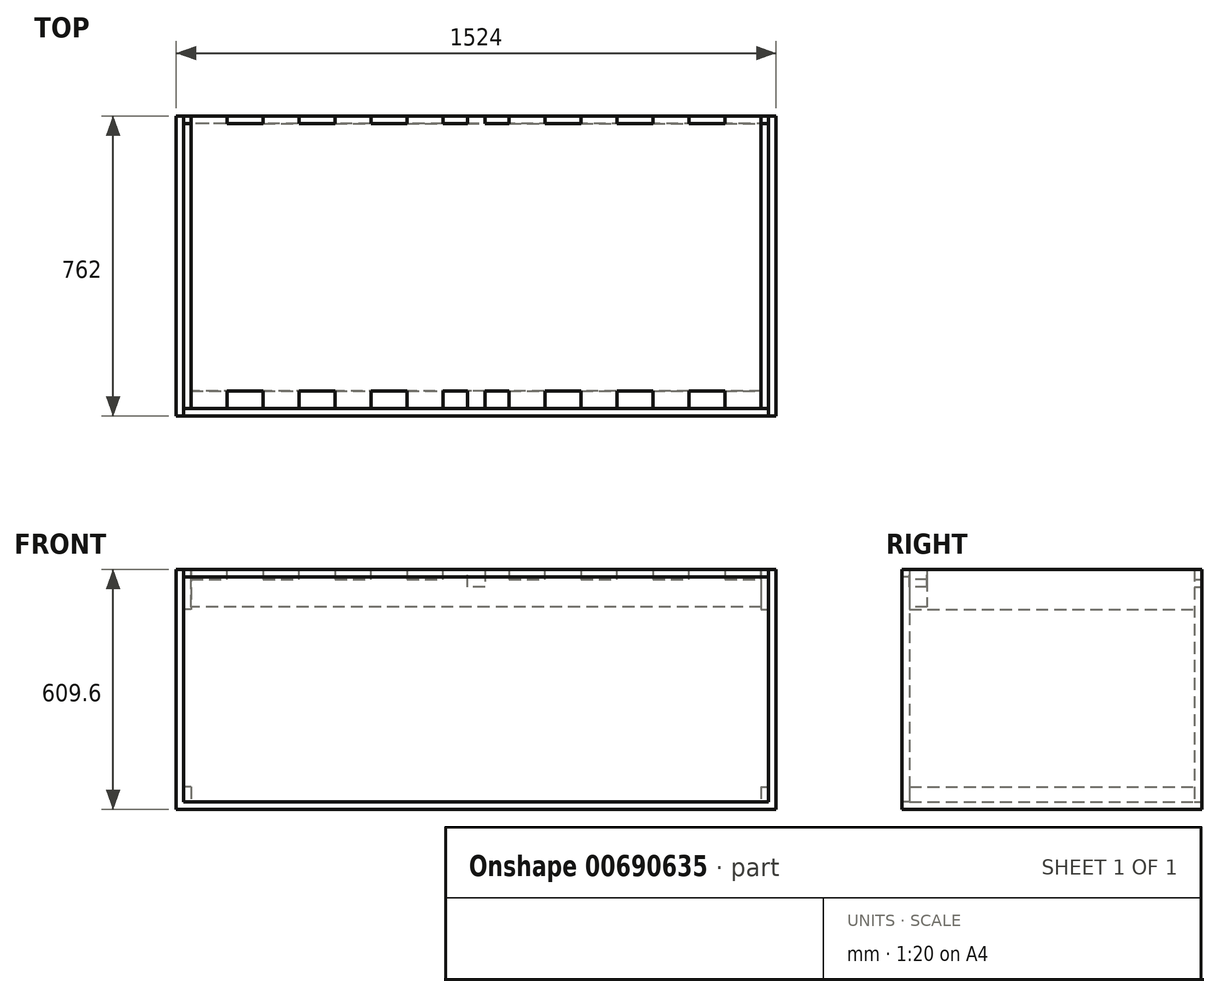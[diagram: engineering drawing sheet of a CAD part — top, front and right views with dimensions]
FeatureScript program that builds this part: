
annotation { "Feature Type Name" : "Feature", "Feature Type Description" : "" }
export const myFeature = defineFeature(function(context is Context, id is Id, definition is map)
    precondition{}
    {
        {
            var Q0;
            Q0=qCreatedBy(makeId("Top.planeOp"),FACE);
            var sketch = newSketch(context, id + "F0", { "sketchPlane" : qUnion([Q0])});
            skLineSegment(sketch, "E0.bottom", {"start": v(-762, -381) * mm, "end": v(762, -381) * mm});
            skLineSegment(sketch, "E0.top", {"start": v(-762, 381) * mm, "end": v(762, 381) * mm});
            skLineSegment(sketch, "E0.left", {"start": v(-762, -381) * mm, "end": v(-762, 381) * mm});
            skLineSegment(sketch, "E0.right", {"start": v(762, -381) * mm, "end": v(762, 381) * mm});
            skPoint(sketch, "E0.middle", {"position": v(0, 0) * mm});
            skSolve(sketch);
        }
        {
            var Q0;
            Q0=makeQuery(id+"F0.imprint","IMPRINT",FACE,{"disambiguationData":[TD([[makeQuery(id+"F0.imprint","IMPRINT",EDGE,{"derivedFrom":sQuery(id+"F0.wireOp",EDGE,"E0.bottom")}),1.0]])]});
            extrude(context, id + "F1", {"entities" : qUnion([Q0]), "oppositeDirection" : true, "depth" : 609.6 * mm, "offsetDistance" : 25.4 * mm});
        }
        {
            var Q0;
            Q0=makeQuery(id+"F1.opExtrude","SWEPT_FACE",FACE,{"disambiguationData":[OSD([sQuery(id+"F0.wireOp",EDGE,"E0.bottom")])]});
            var sketch = newSketch(context, id + "F2", { "sketchPlane" : qUnion([Q0])});
            skLineSegment(sketch, "E1.bottom", {"start": v(-742.95, -19.05) * mm, "end": v(742.95, -19.05) * mm});
            skLineSegment(sketch, "E1.top", {"start": v(-742.95, -590.55) * mm, "end": v(742.95, -590.55) * mm});
            skLineSegment(sketch, "E1.left", {"start": v(-742.95, -19.05) * mm, "end": v(-742.95, -590.55) * mm});
            skLineSegment(sketch, "E1.right", {"start": v(742.95, -19.05) * mm, "end": v(742.95, -590.55) * mm});
            skSolve(sketch);
        }
        {
            var Q0;
            Q0 = qSketchRegion(id + "F2", true);
            extrude(context, id + "F3", {"entities" : qUnion([Q0]), "oppositeDirection" : true, "depth" : 19.05 * mm, "offsetDistance" : 25.4 * mm});
        }
        {
            var Q0;
            Q0=makeQuery(id+"F3.opExtrude","CAP_FACE",FACE,{"disambiguationData":[OSD([sQuery(id+"F2.wireOp",EDGE,"E1.bottom"),sQuery(id+"F2.wireOp",EDGE,"E1.top"),sQuery(id+"F2.wireOp",EDGE,"E1.left"),sQuery(id+"F2.wireOp",EDGE,"E1.right")])],"isStart":false});
            var sketch = newSketch(context, id + "F4", { "sketchPlane" : qUnion([Q0])});
            skLineSegment(sketch, "E2", {"start": v(-723.9, -95.25) * mm, "end": v(723.9, -95.25) * mm});
            skLineSegment(sketch, "E3", {"start": v(723.9, -95.25) * mm, "end": v(723.9, -25.4) * mm});
            skLineSegment(sketch, "E4", {"start": v(723.9, -25.4) * mm, "end": v(632.46, -25.4) * mm});
            skLineSegment(sketch, "E5", {"start": v(632.46, -25.4) * mm, "end": v(632.46, 0) * mm});
            skLineSegment(sketch, "E6", {"start": v(632.46, 0) * mm, "end": v(541.02, 0) * mm});
            skLineSegment(sketch, "E7", {"start": v(541.02, 0) * mm, "end": v(541.02, -25.4) * mm});
            skLineSegment(sketch, "E8", {"start": v(541.02, -25.4) * mm, "end": v(449.58, -25.4) * mm});
            skLineSegment(sketch, "E9", {"start": v(449.58, -25.4) * mm, "end": v(449.58, 0) * mm});
            skLineSegment(sketch, "E10", {"start": v(449.58, 0) * mm, "end": v(358.14, 0) * mm});
            skLineSegment(sketch, "E11", {"start": v(358.14, 0) * mm, "end": v(358.14, -25.4) * mm});
            skLineSegment(sketch, "E12", {"start": v(358.14, -25.4) * mm, "end": v(266.7, -25.4) * mm});
            skLineSegment(sketch, "E13", {"start": v(266.7, -25.4) * mm, "end": v(266.7, 0) * mm});
            skLineSegment(sketch, "E14", {"start": v(266.7, 0) * mm, "end": v(175.26, 0) * mm});
            skLineSegment(sketch, "E15", {"start": v(175.26, 0) * mm, "end": v(175.26, -25.4) * mm});
            skLineSegment(sketch, "E16", {"start": v(175.26, -25.4) * mm, "end": v(83.82, -25.4) * mm});
            skLineSegment(sketch, "E17", {"start": v(83.82, -25.4) * mm, "end": v(83.82, 0) * mm});
            skLineSegment(sketch, "E18", {"start": v(-83.82, 0) * mm, "end": v(-83.82, -25.4) * mm});
            skLineSegment(sketch, "E19", {"start": v(-83.82, -25.4) * mm, "end": v(-175.26, -25.4) * mm});
            skLineSegment(sketch, "E20", {"start": v(-175.26, -25.4) * mm, "end": v(-175.26, 0) * mm});
            skLineSegment(sketch, "E21", {"start": v(-175.26, 0) * mm, "end": v(-266.7, 0) * mm});
            skLineSegment(sketch, "E22", {"start": v(-266.7, 0) * mm, "end": v(-266.7, -25.4) * mm});
            skLineSegment(sketch, "E23", {"start": v(-266.7, -25.4) * mm, "end": v(-358.14, -25.4) * mm});
            skLineSegment(sketch, "E24", {"start": v(-358.14, -25.4) * mm, "end": v(-358.14, 0) * mm});
            skLineSegment(sketch, "E25", {"start": v(-358.14, 0) * mm, "end": v(-449.58, 0) * mm});
            skLineSegment(sketch, "E26", {"start": v(-449.58, 0) * mm, "end": v(-449.58, -25.4) * mm});
            skLineSegment(sketch, "E27", {"start": v(-449.58, -25.4) * mm, "end": v(-541.02, -25.4) * mm});
            skLineSegment(sketch, "E28", {"start": v(-541.02, -25.4) * mm, "end": v(-541.02, 0) * mm});
            skLineSegment(sketch, "E29", {"start": v(-541.02, 0) * mm, "end": v(-632.46, 0) * mm});
            skLineSegment(sketch, "E30", {"start": v(-632.46, 0) * mm, "end": v(-632.46, -25.4) * mm});
            skLineSegment(sketch, "E31", {"start": v(-632.46, -25.4) * mm, "end": v(-723.9, -25.4) * mm});
            skLineSegment(sketch, "E32", {"start": v(-723.9, -25.4) * mm, "end": v(-723.9, -95.25) * mm});
            skLineSegment(sketch, "E33", {"start": v(-83.82, 0) * mm, "end": v(-22.22, 0) * mm});
            skLineSegment(sketch, "E34", {"start": v(-22.22, 0) * mm, "end": v(-22.22, -44.45) * mm});
            skLineSegment(sketch, "E35", {"start": v(-22.22, -44.45) * mm, "end": v(22.23, -44.45) * mm});
            skLineSegment(sketch, "E36", {"start": v(22.23, -44.45) * mm, "end": v(22.23, 0) * mm});
            skLineSegment(sketch, "E37", {"start": v(22.23, 0) * mm, "end": v(83.82, 0) * mm});
            skSolve(sketch);
        }
        {
            var Q0;
            Q0 = qSketchRegion(id + "F4", true);
            extrude(context, id + "F5", {"entities" : qUnion([Q0]), "depth" : 44.45 * mm, "offsetDistance" : 25.4 * mm});
        }
        {
            var Q0;
            Q0=makeQuery(id+"F1.opExtrude","SWEPT_FACE",FACE,{"disambiguationData":[OSD([sQuery(id+"F0.wireOp",EDGE,"E0.top")])]});
            var sketch = newSketch(context, id + "F6", { "sketchPlane" : qUnion([Q0])});
            skLineSegment(sketch, "E38", {"start": v(-742.95, -590.55) * mm, "end": v(742.95, -590.55) * mm});
            skLineSegment(sketch, "E39", {"start": v(742.95, -590.55) * mm, "end": v(742.95, 0) * mm});
            skLineSegment(sketch, "E40", {"start": v(632.46, -25.4) * mm, "end": v(632.46, 0) * mm});
            skLineSegment(sketch, "E41", {"start": v(632.46, 0) * mm, "end": v(541.02, 0) * mm});
            skLineSegment(sketch, "E42", {"start": v(541.02, 0) * mm, "end": v(541.02, -25.4) * mm});
            skLineSegment(sketch, "E43", {"start": v(541.02, -25.4) * mm, "end": v(449.58, -25.4) * mm});
            skLineSegment(sketch, "E44", {"start": v(449.58, -25.4) * mm, "end": v(449.58, 0) * mm});
            skLineSegment(sketch, "E45", {"start": v(449.58, 0) * mm, "end": v(358.14, 0) * mm});
            skLineSegment(sketch, "E46", {"start": v(358.14, 0) * mm, "end": v(358.14, -25.4) * mm});
            skLineSegment(sketch, "E47", {"start": v(358.14, -25.4) * mm, "end": v(266.7, -25.4) * mm});
            skLineSegment(sketch, "E48", {"start": v(266.7, -25.4) * mm, "end": v(266.7, 0) * mm});
            skLineSegment(sketch, "E49", {"start": v(266.7, 0) * mm, "end": v(175.26, 0) * mm});
            skLineSegment(sketch, "E50", {"start": v(175.26, 0) * mm, "end": v(175.26, -25.4) * mm});
            skLineSegment(sketch, "E51", {"start": v(175.26, -25.4) * mm, "end": v(83.82, -25.4) * mm});
            skLineSegment(sketch, "E52", {"start": v(83.82, -25.4) * mm, "end": v(83.82, 0) * mm});
            skLineSegment(sketch, "E53", {"start": v(83.82, 0) * mm, "end": v(22.23, 0) * mm});
            skLineSegment(sketch, "E54", {"start": v(22.23, 0) * mm, "end": v(22.23, -44.45) * mm});
            skLineSegment(sketch, "E55", {"start": v(22.23, -44.45) * mm, "end": v(-22.22, -44.45) * mm});
            skLineSegment(sketch, "E56", {"start": v(-22.22, -44.45) * mm, "end": v(-22.22, 0) * mm});
            skLineSegment(sketch, "E57", {"start": v(-22.22, 0) * mm, "end": v(-83.82, 0) * mm});
            skLineSegment(sketch, "E58", {"start": v(-83.82, 0) * mm, "end": v(-83.82, -25.4) * mm});
            skLineSegment(sketch, "E59", {"start": v(-83.82, -25.4) * mm, "end": v(-175.26, -25.4) * mm});
            skLineSegment(sketch, "E60", {"start": v(-175.26, -25.4) * mm, "end": v(-175.26, 0) * mm});
            skLineSegment(sketch, "E61", {"start": v(-175.26, 0) * mm, "end": v(-266.7, 0) * mm});
            skLineSegment(sketch, "E62", {"start": v(-266.7, 0) * mm, "end": v(-266.7, -25.4) * mm});
            skLineSegment(sketch, "E63", {"start": v(-266.7, -25.4) * mm, "end": v(-358.14, -25.4) * mm});
            skLineSegment(sketch, "E64", {"start": v(-358.14, -25.4) * mm, "end": v(-358.14, 0) * mm});
            skLineSegment(sketch, "E65", {"start": v(-358.14, 0) * mm, "end": v(-449.58, 0) * mm});
            skLineSegment(sketch, "E66", {"start": v(-449.58, 0) * mm, "end": v(-449.58, -25.4) * mm});
            skLineSegment(sketch, "E67", {"start": v(-449.58, -25.4) * mm, "end": v(-541.02, -25.4) * mm});
            skLineSegment(sketch, "E68", {"start": v(-541.02, -25.4) * mm, "end": v(-541.02, 0) * mm});
            skLineSegment(sketch, "E69", {"start": v(-541.02, 0) * mm, "end": v(-632.46, 0) * mm});
            skLineSegment(sketch, "E70", {"start": v(-632.46, 0) * mm, "end": v(-632.46, -25.4) * mm});
            skLineSegment(sketch, "E71", {"start": v(-742.95, 0) * mm, "end": v(-742.95, -590.55) * mm});
            skLineSegment(sketch, "E72", {"start": v(-632.46, -25.4) * mm, "end": v(-723.9, -25.4) * mm});
            skLineSegment(sketch, "E73", {"start": v(-723.9, -25.4) * mm, "end": v(-723.9, 0) * mm});
            skLineSegment(sketch, "E74", {"start": v(-723.9, 0) * mm, "end": v(-742.95, 0) * mm});
            skLineSegment(sketch, "E75", {"start": v(632.46, -25.4) * mm, "end": v(723.9, -25.4) * mm});
            skLineSegment(sketch, "E76", {"start": v(723.9, -25.4) * mm, "end": v(723.9, 0) * mm});
            skLineSegment(sketch, "E77", {"start": v(723.9, 0) * mm, "end": v(742.95, 0) * mm});
            skSolve(sketch);
        }
        {
            var Q0;
            Q0 = qSketchRegion(id + "F6", true);
            extrude(context, id + "F7", {"entities" : qUnion([Q0]), "oppositeDirection" : true, "depth" : 19.05 * mm, "offsetDistance" : 25.4 * mm});
        }
        {
            var Q0;
            Q0=makeQuery(id+"F3.opExtrude","SWEPT_FACE",FACE,{"disambiguationData":[OSD([sQuery(id+"F2.wireOp",EDGE,"E1.right")])]});
            var sketch = newSketch(context, id + "F8", { "sketchPlane" : qUnion([Q0])});
            skLineSegment(sketch, "E78.bottom", {"start": v(-361.95, 0) * mm, "end": v(361.95, 0) * mm});
            skLineSegment(sketch, "E78.top", {"start": v(-361.95, -101.6) * mm, "end": v(361.95, -101.6) * mm});
            skLineSegment(sketch, "E78.left", {"start": v(-361.95, 0) * mm, "end": v(-361.95, -101.6) * mm});
            skLineSegment(sketch, "E78.right", {"start": v(361.95, 0) * mm, "end": v(361.95, -101.6) * mm});
            skLineSegment(sketch, "E79.bottom", {"start": v(-361.95, -552.45) * mm, "end": v(361.95, -552.45) * mm});
            skLineSegment(sketch, "E79.top", {"start": v(-361.95, -590.55) * mm, "end": v(361.95, -590.55) * mm});
            skLineSegment(sketch, "E79.left", {"start": v(-361.95, -552.45) * mm, "end": v(-361.95, -590.55) * mm});
            skLineSegment(sketch, "E79.right", {"start": v(361.95, -552.45) * mm, "end": v(361.95, -590.55) * mm});
            skSolve(sketch);
        }
        {
            var Q0;
            Q0 = qSketchRegion(id + "F8", true);
            extrude(context, id + "F9", {"entities" : qUnion([Q0]), "oppositeDirection" : true, "depth" : 19.05 * mm, "offsetDistance" : 25.4 * mm});
        }
        {
            var Q0;
            Q0=makeQuery(id+"F9.opExtrude","SWEPT_BODY",BODY,{"disambiguationData":[OSD([sQuery(id+"F8.wireOp",EDGE,"E78.bottom"),sQuery(id+"F8.wireOp",EDGE,"E78.top"),sQuery(id+"F8.wireOp",EDGE,"E78.left"),sQuery(id+"F8.wireOp",EDGE,"E78.right")])]});
            var Q1;
            Q1=makeQuery(id+"F9.opExtrude","SWEPT_BODY",BODY,{"disambiguationData":[OSD([sQuery(id+"F8.wireOp",EDGE,"E79.bottom"),sQuery(id+"F8.wireOp",EDGE,"E79.top"),sQuery(id+"F8.wireOp",EDGE,"E79.left"),sQuery(id+"F8.wireOp",EDGE,"E79.right")])]});
            var Q2;
            Q2=qCreatedBy(makeId("Right.planeOp"),FACE);
            mirror(context, id + "F10", {"entities" : qUnion([Q0, Q1]), "mirrorPlane" : qUnion([Q2])});
        }
        {
            var Q0;
            Q0=makeQuery(id+"F3.opExtrude","SWEPT_FACE",FACE,{"disambiguationData":[OSD([sQuery(id+"F2.wireOp",EDGE,"E1.bottom")])]});
            var sketch = newSketch(context, id + "F11", { "sketchPlane" : qUnion([Q0])});
            skLineSegment(sketch, "E80.bottom", {"start": v(-742.95, -381) * mm, "end": v(742.95, -381) * mm});
            skLineSegment(sketch, "E80.top", {"start": v(-742.95, -361.95) * mm, "end": v(742.95, -361.95) * mm});
            skLineSegment(sketch, "E80.left", {"start": v(-742.95, -381) * mm, "end": v(-742.95, -361.95) * mm});
            skLineSegment(sketch, "E80.right", {"start": v(742.95, -381) * mm, "end": v(742.95, -361.95) * mm});
            skSolve(sketch);
        }
        {
            var Q0;
            Q0 = qSketchRegion(id + "F11", true);
            extrude(context, id + "F12", {"entities" : qUnion([Q0]), "depth" : 19.05 * mm, "offsetDistance" : 25.4 * mm});
        }
    });
